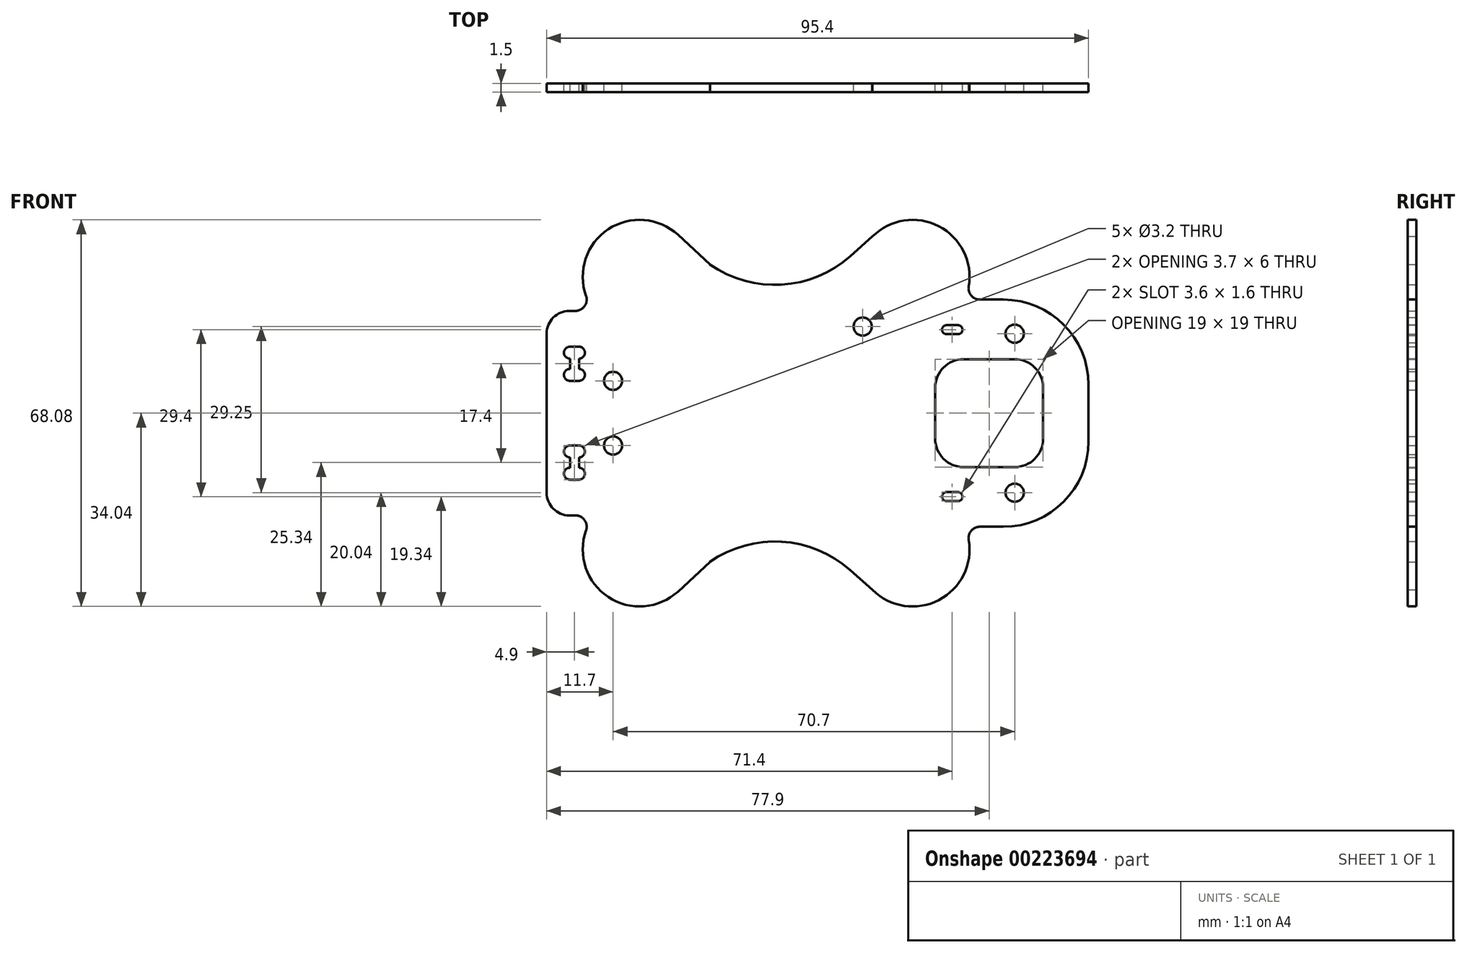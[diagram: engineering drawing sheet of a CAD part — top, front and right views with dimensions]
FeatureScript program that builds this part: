
annotation { "Feature Type Name" : "Feature", "Feature Type Description" : "" }
export const myFeature = defineFeature(function(context is Context, id is Id, definition is map)
    precondition{}
    {
        {
            var Q0;
            Q0=qCreatedBy(makeId("Front.planeOp"),FACE);
            var sketch = newSketch(context, id + "F0", { "sketchPlane" : qUnion([Q0])});
            skPoint(sketch, "E0", {"position": v(0, 0) * mm});
            skCircle(sketch, "E1", {"center": v(15.25, 15.25) * mm, "radius": 1.6 * mm});
            skLineSegment(sketch, "E2", {"start": v(-25.7, -25.7) * mm, "end": v(60.72, 60.72) * mm, "construction": true});
            skLineSegment(sketch, "E3", {"start": v(16.97, 31.11) * mm, "end": v(13.1, 27.66) * mm});
            skLineSegment(sketch, "E4", {"start": v(0, -54.73) * mm, "end": v(0, 66.02) * mm, "construction": true});
            skPoint(sketch, "E5.visualSharp", {"position": v(0, 16) * mm});
            skArc(sketch, "E5.filletArc", {"start": v(-11.66, 26.2) * mm, "mid": v(0.97, 22.63) * mm, "end": v(13.1, 27.66) * mm});
            skLineSegment(sketch, "E6.bottom", {"start": v(-34.7, 5.7) * mm, "end": v(-36.3, 5.7) * mm});
            skLineSegment(sketch, "E6.top", {"start": v(-34.7, 11.7) * mm, "end": v(-36.3, 11.7) * mm});
            skLineSegment(sketch, "E6.right", {"start": v(-36.3, 7.8) * mm, "end": v(-36.3, 9.6) * mm});
            skArc(sketch, "E7", {"start": v(-36.3, 11.7) * mm, "mid": v(-37.35, 10.65) * mm, "end": v(-36.3, 9.6) * mm});
            skArc(sketch, "E8", {"start": v(-34.7, 9.6) * mm, "mid": v(-33.65, 10.65) * mm, "end": v(-34.7, 11.7) * mm});
            skArc(sketch, "E9", {"start": v(-36.3, 7.8) * mm, "mid": v(-37.35, 6.75) * mm, "end": v(-36.3, 5.7) * mm});
            skArc(sketch, "E10", {"start": v(-34.7, 5.7) * mm, "mid": v(-33.65, 6.75) * mm, "end": v(-34.7, 7.8) * mm});
            skLineSegment(sketch, "E11.trimOffspring", {"start": v(-34.7, 7.8) * mm, "end": v(-34.7, 9.6) * mm});
            skLineSegment(sketch, "E12.MirrorCS", {"start": v(-34.7, -11.7) * mm, "end": v(-36.3, -11.7) * mm});
            skLineSegment(sketch, "E13.MirrorCS", {"start": v(-34.7, -5.7) * mm, "end": v(-36.3, -5.7) * mm});
            skLineSegment(sketch, "E14.MirrorCS", {"start": v(-36.3, -7.8) * mm, "end": v(-36.3, -9.6) * mm});
            skLineSegment(sketch, "E15.MirrorCS", {"start": v(-34.7, -7.8) * mm, "end": v(-34.7, -9.6) * mm});
            skArc(sketch, "E16.MirrorCS", {"start": v(-36.3, -7.8) * mm, "mid": v(-37.35, -6.75) * mm, "end": v(-36.3, -5.7) * mm});
            skArc(sketch, "E17.MirrorCS", {"start": v(-34.7, -5.7) * mm, "mid": v(-33.65, -6.75) * mm, "end": v(-34.7, -7.8) * mm});
            skArc(sketch, "E18.MirrorCS", {"start": v(-34.7, -9.6) * mm, "mid": v(-33.65, -10.65) * mm, "end": v(-34.7, -11.7) * mm});
            skArc(sketch, "E19.MirrorCS", {"start": v(-36.3, -11.7) * mm, "mid": v(-37.35, -10.65) * mm, "end": v(-36.3, -9.6) * mm});
            skLineSegment(sketch, "E20", {"start": v(87.03, 0) * mm, "end": v(-68.93, 0) * mm, "construction": true});
            skLineSegment(sketch, "E21", {"start": v(-40.4, 0) * mm, "end": v(-40.4, 14) * mm});
            skLineSegment(sketch, "E22", {"start": v(-35.34, 18) * mm, "end": v(-36.4, 18) * mm});
            skPoint(sketch, "E23.visualSharp", {"position": v(-30.08, 18) * mm});
            skPoint(sketch, "E24.visualSharp", {"position": v(-40.4, 18) * mm});
            skArc(sketch, "E24.filletArc", {"start": v(-36.4, 18) * mm, "mid": v(-39.23, 16.83) * mm, "end": v(-40.4, 14) * mm});
            skLineSegment(sketch, "E25", {"start": v(55, 5) * mm, "end": v(55, 0) * mm});
            skLineSegment(sketch, "E26.MirrorCS", {"start": v(-40.4, 0) * mm, "end": v(-40.4, -14) * mm});
            skArc(sketch, "E27.MirrorCS", {"start": v(-36.4, -18) * mm, "mid": v(-39.23, -16.83) * mm, "end": v(-40.4, -14) * mm});
            skCircle(sketch, "E28", {"center": v(42, 14) * mm, "radius": 1.6 * mm});
            skLineSegment(sketch, "E29", {"start": v(40, 20) * mm, "end": v(35.87, 20) * mm});
            skPoint(sketch, "E30.visualSharp", {"position": v(55, 20) * mm});
            skArc(sketch, "E30.filletArc", {"start": v(55, 5) * mm, "mid": v(50.6, 15.6) * mm, "end": v(40, 20) * mm});
            skCircle(sketch, "E31.MirrorC", {"center": v(42, -14) * mm, "radius": 1.6 * mm});
            skLineSegment(sketch, "E32.MirrorCS", {"start": v(55, -5) * mm, "end": v(55, 0) * mm});
            skArc(sketch, "E33.MirrorCS", {"start": v(55, -5) * mm, "mid": v(50.6, -15.6) * mm, "end": v(40, -20) * mm});
            skLineSegment(sketch, "E34", {"start": v(28, 0) * mm, "end": v(28, 4.5) * mm});
            skLineSegment(sketch, "E35", {"start": v(33, 9.5) * mm, "end": v(42, 9.5) * mm});
            skLineSegment(sketch, "E36", {"start": v(47, 4.5) * mm, "end": v(47, 0) * mm});
            skPoint(sketch, "E37.visualSharp", {"position": v(28, 9.5) * mm});
            skArc(sketch, "E37.filletArc", {"start": v(33, 9.5) * mm, "mid": v(29.46, 8.04) * mm, "end": v(28, 4.5) * mm});
            skPoint(sketch, "E38.visualSharp", {"position": v(47, 9.5) * mm});
            skArc(sketch, "E38.filletArc", {"start": v(47, 4.5) * mm, "mid": v(45.54, 8.04) * mm, "end": v(42, 9.5) * mm});
            skLineSegment(sketch, "E39.MirrorCS", {"start": v(47, -4.5) * mm, "end": v(47, 0) * mm});
            skArc(sketch, "E40.MirrorCS", {"start": v(47, -4.5) * mm, "mid": v(45.54, -8.04) * mm, "end": v(42, -9.5) * mm});
            skLineSegment(sketch, "E41.MirrorCS", {"start": v(28, 0) * mm, "end": v(28, -4.5) * mm});
            skLineSegment(sketch, "E42.MirrorCS", {"start": v(33, -9.5) * mm, "end": v(42, -9.5) * mm});
            skArc(sketch, "E43.MirrorCS", {"start": v(33, -9.5) * mm, "mid": v(29.46, -8.04) * mm, "end": v(28, -4.5) * mm});
            skCircle(sketch, "E44", {"center": v(-28.7, 5.7) * mm, "radius": 1.6 * mm});
            skCircle(sketch, "E45.MirrorC", {"center": v(-28.7, -5.7) * mm, "radius": 1.6 * mm});
            skLineSegment(sketch, "E46.bottom", {"start": v(30, 15.5) * mm, "end": v(32, 15.5) * mm});
            skLineSegment(sketch, "E46.top", {"start": v(30, 13.9) * mm, "end": v(32, 13.9) * mm});
            skArc(sketch, "E47", {"start": v(32, 13.9) * mm, "mid": v(32.8, 14.7) * mm, "end": v(32, 15.5) * mm});
            skArc(sketch, "E48", {"start": v(30, 15.5) * mm, "mid": v(29.2, 14.7) * mm, "end": v(30, 13.9) * mm});
            skPoint(sketch, "E49.left.end.orphan", {"position": v(30, 13.9) * mm});
            skPoint(sketch, "E50.MirrorP", {"position": v(30, -13.9) * mm});
            skArc(sketch, "E51.MirrorCS", {"start": v(32, -13.9) * mm, "mid": v(32.8, -14.7) * mm, "end": v(32, -15.5) * mm});
            skArc(sketch, "E52.MirrorCS", {"start": v(30, -15.5) * mm, "mid": v(29.2, -14.7) * mm, "end": v(30, -13.9) * mm});
            skLineSegment(sketch, "E53.MirrorCS", {"start": v(30, -13.9) * mm, "end": v(32, -13.9) * mm});
            skLineSegment(sketch, "E54.MirrorCS", {"start": v(30, -15.5) * mm, "end": v(32, -15.5) * mm});
            skArc(sketch, "E55", {"start": v(33.9, 22.34) * mm, "mid": v(28.64, 32.92) * mm, "end": v(16.97, 31.11) * mm});
            skArc(sketch, "E56.filletArc", {"start": v(33.9, 22.34) * mm, "mid": v(34.34, 20.71) * mm, "end": v(35.87, 20) * mm});
            skLineSegment(sketch, "E57", {"start": v(0, 0) * mm, "end": v(-33.9, 33.9) * mm, "construction": true});
            skArc(sketch, "E58", {"start": v(-17.25, 31.38) * mm, "mid": v(-29.55, 32.39) * mm, "end": v(-33.46, 20.67) * mm});
            skLineSegment(sketch, "E59", {"start": v(-11.66, 26.2) * mm, "end": v(-17.25, 31.38) * mm});
            skPoint(sketch, "E60.visualSharp", {"position": v(-32.01, 18) * mm});
            skArc(sketch, "E60.filletArc", {"start": v(-35.34, 18) * mm, "mid": v(-33.7, 18.85) * mm, "end": v(-33.46, 20.67) * mm});
            skLineSegment(sketch, "E61.MirrorCS", {"start": v(40, -20) * mm, "end": v(35.87, -20) * mm});
            skArc(sketch, "E62.MirrorCS", {"start": v(33.9, -22.34) * mm, "mid": v(34.34, -20.71) * mm, "end": v(35.87, -20) * mm});
            skArc(sketch, "E63.MirrorCS", {"start": v(33.9, -22.34) * mm, "mid": v(28.64, -32.92) * mm, "end": v(16.97, -31.11) * mm});
            skLineSegment(sketch, "E64.MirrorCS", {"start": v(16.97, -31.11) * mm, "end": v(13.1, -27.66) * mm});
            skArc(sketch, "E65.MirrorCS", {"start": v(-11.66, -26.2) * mm, "mid": v(0.97, -22.63) * mm, "end": v(13.1, -27.66) * mm});
            skLineSegment(sketch, "E66.MirrorCS", {"start": v(-35.34, -18) * mm, "end": v(-36.4, -18) * mm});
            skLineSegment(sketch, "E67.MirrorCS", {"start": v(-11.66, -26.2) * mm, "end": v(-17.25, -31.38) * mm});
            skArc(sketch, "E68.MirrorCS", {"start": v(-35.34, -18) * mm, "mid": v(-33.7, -18.85) * mm, "end": v(-33.46, -20.67) * mm});
            skArc(sketch, "E69.MirrorCS", {"start": v(-17.25, -31.38) * mm, "mid": v(-29.55, -32.39) * mm, "end": v(-33.46, -20.67) * mm});
            skSolve(sketch);
        }
        {
            var Q0;
            Q0=qSketchRegion(id+"F0",true);
            extrude(context, id + "F1", {"entities" : qUnion([Q0]), "depth" : 1.5 * mm});
        }
    });
